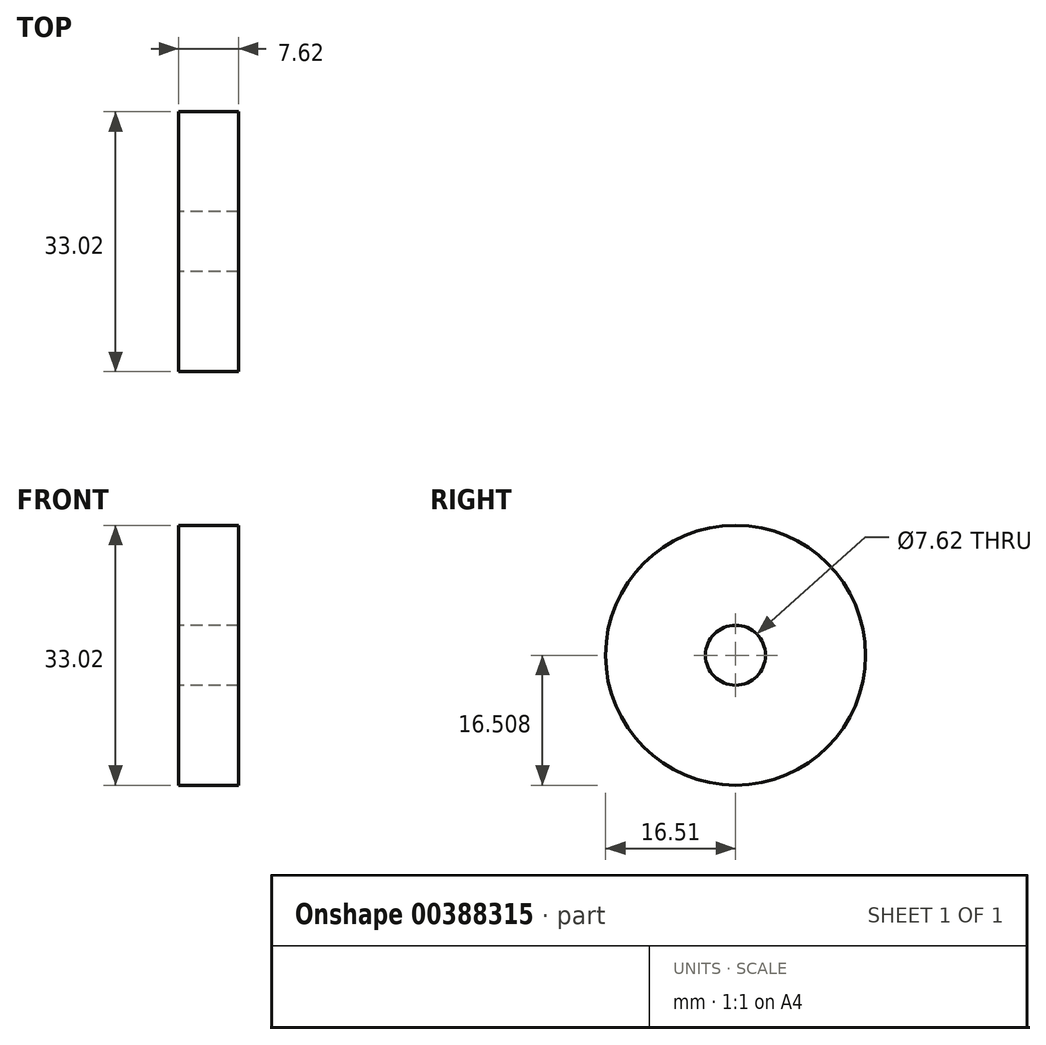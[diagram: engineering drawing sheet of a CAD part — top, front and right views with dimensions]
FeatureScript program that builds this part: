
annotation { "Feature Type Name" : "Feature", "Feature Type Description" : "" }
export const myFeature = defineFeature(function(context is Context, id is Id, definition is map)
    precondition{}
    {
        {
            var Q0;
            Q0=qCreatedBy(makeId("Front.planeOp"),FACE);
            var sketch = newSketch(context, id + "F0", { "sketchPlane" : qUnion([Q0])});
            skLineSegment(sketch, "E0", {"start": v(-0.88, 34.14) * mm, "end": v(6.74, 34.14) * mm});
            skLineSegment(sketch, "E1", {"start": v(6.74, 34.14) * mm, "end": v(6.74, 17.63) * mm});
            skLineSegment(sketch, "E2", {"start": v(6.74, 17.63) * mm, "end": v(-0.88, 17.63) * mm});
            skLineSegment(sketch, "E3", {"start": v(-0.88, 17.63) * mm, "end": v(-0.88, 34.14) * mm});
            skSolve(sketch);
        }
        {
            var Q0;
            Q0=qSketchRegion(id+"F0",true);
            var Q1;
            Q1=sQuery(id+"F0.wireOp",EDGE,"E2");
            revolve(context, id + "F1", {"entities" : qUnion([Q0]), "axis" : qUnion([Q1]), "revolveType" : RevolveType.FULL});
        }
        {
            var Q0;
            Q0=makeQuery(id+"F1.opRevolve","SWEPT_FACE",FACE,{"disambiguationData":[OSD([sQuery(id+"F0.wireOp",EDGE,"E3")])]});
            var sketch = newSketch(context, id + "F2", { "sketchPlane" : qUnion([Q0])});
            skCircle(sketch, "E4", {"center": v(0, 17.63) * mm, "radius": 3.81 * mm});
            skSolve(sketch);
        }
        {
            var Q0;
            Q0=qSketchRegion(id+"F2",true);
            extrude(context, id + "F3", {"entities" : qUnion([Q0]), "operationType" : NewBodyOperationType.REMOVE, "oppositeDirection" : true, "depth" : 25.4 * mm});
        }
    });
